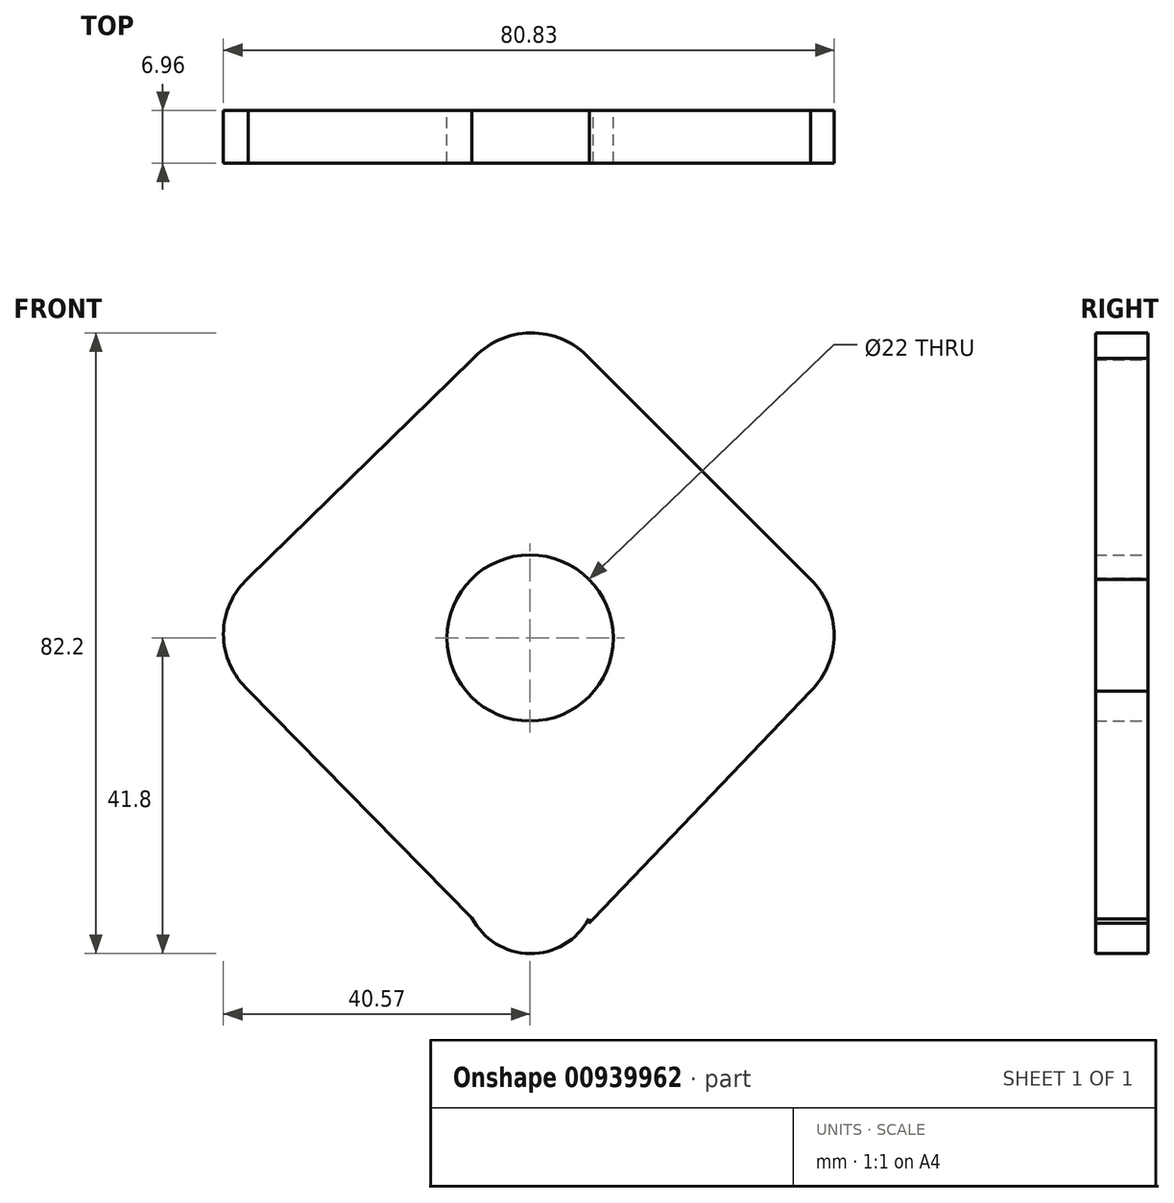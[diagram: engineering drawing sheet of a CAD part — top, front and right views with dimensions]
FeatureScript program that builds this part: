
annotation { "Feature Type Name" : "Feature", "Feature Type Description" : "" }
export const myFeature = defineFeature(function(context is Context, id is Id, definition is map)
    precondition{}
    {
        {
            var Q0;
            Q0=qCreatedBy(makeId("Front.planeOp"),FACE);
            var sketch = newSketch(context, id + "F0", { "sketchPlane" : qUnion([Q0])});
            skArc(sketch, "E0", {"start": v(-8.47, -7.02) * mm, "mid": v(-8.12, -7.42) * mm, "end": v(-7.76, -7.8) * mm});
            skArc(sketch, "E1.trimOffspring", {"start": v(7.76, -7.8) * mm, "mid": v(8.12, -7.42) * mm, "end": v(8.47, -7.02) * mm});
            skPoint(sketch, "E2.end.orphan", {"position": v(-35.25, 10.65) * mm});
            skPoint(sketch, "E2.start.orphan", {"position": v(-37.26, 10.65) * mm});
            skArc(sketch, "E3", {"start": v(-7.76, -7.8) * mm, "mid": v(8.12, 7.42) * mm, "end": v(-8.47, -7.02) * mm});
            skLineSegment(sketch, "E4", {"start": v(7.76, -37.8) * mm, "end": v(7.76, -37.19) * mm});
            skPoint(sketch, "E5.start.orphan", {"position": v(7.76, -10.62) * mm});
            skArc(sketch, "E6", {"start": v(7.86, 37.01) * mm, "mid": v(0.04, 40.4) * mm, "end": v(-7.69, 36.8) * mm});
            skArc(sketch, "E7", {"start": v(-37.26, 7.93) * mm, "mid": v(-40.57, 0.52) * mm, "end": v(-37.26, -6.89) * mm});
            skArc(sketch, "E8", {"start": v(-7.7, -37.05) * mm, "mid": v(0, -41.8) * mm, "end": v(7.76, -37.19) * mm});
            skArc(sketch, "E9", {"start": v(37.13, -7.02) * mm, "mid": v(40.26, 0.37) * mm, "end": v(37.13, 7.76) * mm});
            skLineSegment(sketch, "E10", {"start": v(-7.69, 36.8) * mm, "end": v(-37.26, 7.93) * mm});
            skLineSegment(sketch, "E11", {"start": v(-37.26, -6.89) * mm, "end": v(-7.7, -37.05) * mm});
            skLineSegment(sketch, "E12", {"start": v(6.17, -39.3) * mm, "end": v(8.34, -37.19) * mm});
            skLineSegment(sketch, "E13", {"start": v(8.34, -37.19) * mm, "end": v(37.13, -7.02) * mm});
            skLineSegment(sketch, "E14", {"start": v(37.13, 7.76) * mm, "end": v(7.86, 37.01) * mm});
            skSolve(sketch);
        }
        {
            var Q0;
            {var subQ7=sQuery(id+"F0.wireOp",EDGE,"E0");Q0=makeQuery(id+"F0.imprint","IMPRINT",FACE,{"disambiguationData":[TD([[makeQuery(id+"F0.imprint","IMPRINT",EDGE,{"derivedFrom":subQ7}),-1.0]])]});}
            extrude(context, id + "F1", {"entities" : qUnion([Q0]), "depth" : 6.96 * mm, "offsetDistance" : 25 * mm});
        }
    });
